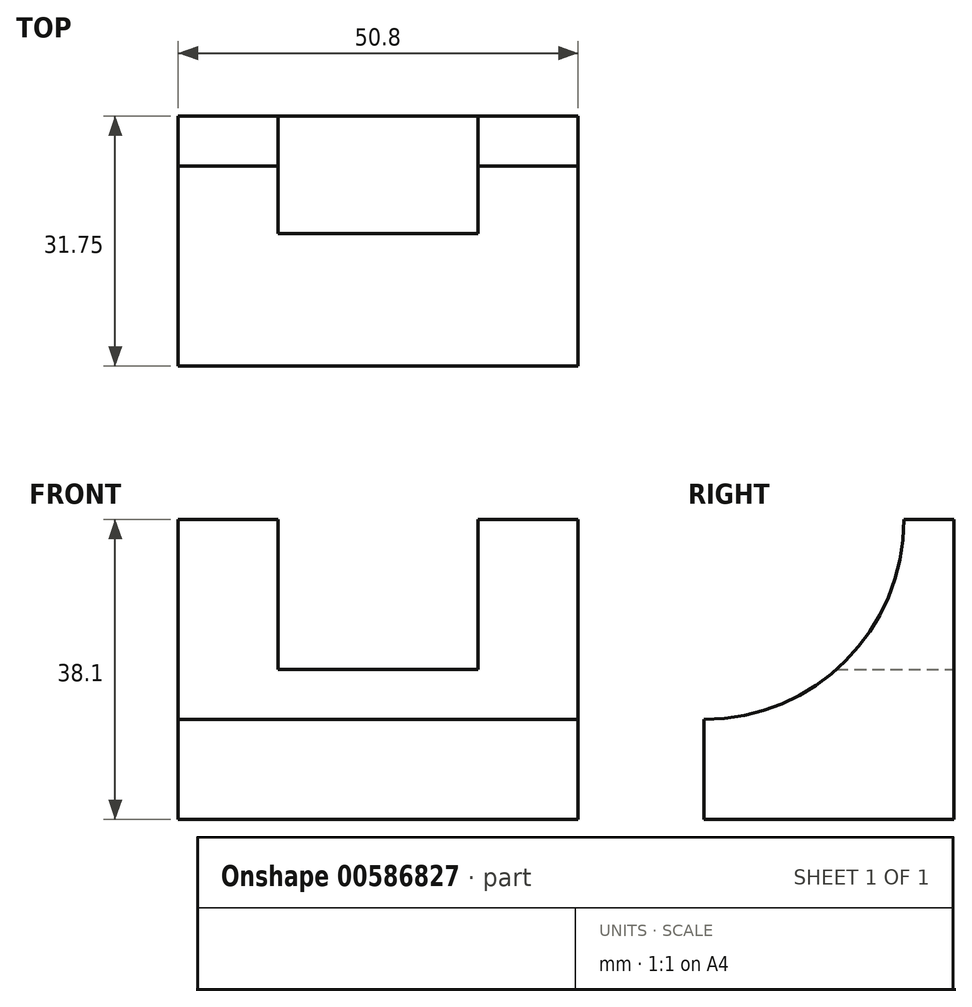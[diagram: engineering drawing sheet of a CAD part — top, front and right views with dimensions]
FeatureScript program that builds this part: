
annotation { "Feature Type Name" : "Feature", "Feature Type Description" : "" }
export const myFeature = defineFeature(function(context is Context, id is Id, definition is map)
    precondition{}
    {
        {
            var Q0;
            Q0=qCreatedBy(makeId("Right.planeOp"),FACE);
            var sketch = newSketch(context, id + "F0", { "sketchPlane" : qUnion([Q0])});
            skLineSegment(sketch, "E0", {"start": v(-49.9, 49.64) * mm, "end": v(-18.16, 49.64) * mm});
            skLineSegment(sketch, "E1", {"start": v(-18.16, 49.64) * mm, "end": v(-18.16, 11.54) * mm});
            skLineSegment(sketch, "E2", {"start": v(-18.16, 11.54) * mm, "end": v(-49.9, 11.54) * mm});
            skLineSegment(sketch, "E3", {"start": v(-49.9, 11.54) * mm, "end": v(-49.9, 49.64) * mm});
            skSolve(sketch);
        }
        {
            var Q0;
            Q0=makeQuery(id+"F0.imprint","IMPRINT",FACE,{"disambiguationData":[TD([[makeQuery(id+"F0.imprint","IMPRINT",EDGE,{"derivedFrom":sQuery(id+"F0.wireOp",EDGE,"E0")}),-1.0]])]});
            extrude(context, id + "F1", {"entities" : qUnion([Q0]), "depth" : 50.8 * mm, "offsetDistance" : 25.4 * mm});
        }
        {
            var Q0;
            Q0=makeQuery(id+"F1.opExtrude","CAP_FACE",FACE,{"disambiguationData":[OSD([sQuery(id+"F0.wireOp",EDGE,"E0"),sQuery(id+"F0.wireOp",EDGE,"E1"),sQuery(id+"F0.wireOp",EDGE,"E2"),sQuery(id+"F0.wireOp",EDGE,"E3")])],"isStart":false});
            var sketch = newSketch(context, id + "F2", { "sketchPlane" : qUnion([Q0])});
            skArc(sketch, "E4", {"start": v(-49.9, 24.24) * mm, "mid": v(-31.95, 31.68) * mm, "end": v(-24.5, 49.64) * mm});
            skSolve(sketch);
        }
        {
            var Q0;
            {var subQ0=sQuery(id+"F2.wireOp",EDGE,"E4");Q0=makeQuery(id+"F2.imprint","IMPRINT",FACE,{"disambiguationData":[TD([[makeQuery(id+"F2.imprint","IMPRINT",EDGE,{"derivedFrom":subQ0}),1.0]])]});}
            extrude(context, id + "F3", {"entities" : qUnion([Q0]), "operationType" : NewBodyOperationType.REMOVE, "endBound" : BoundingType.THROUGH_ALL, "oppositeDirection" : true, "depth" : 25.4 * mm, "offsetDistance" : 25.4 * mm});
        }
        {
            var Q0;
            Q0=makeQuery(id+"F1.opExtrude","SWEPT_FACE",FACE,{"disambiguationData":[OSD([sQuery(id+"F0.wireOp",EDGE,"E1")])]});
            var sketch = newSketch(context, id + "F4", { "sketchPlane" : qUnion([Q0])});
            skLineSegment(sketch, "E5", {"start": v(-38.1, 49.64) * mm, "end": v(-38.1, 30.6) * mm});
            skLineSegment(sketch, "E6", {"start": v(-38.1, 30.6) * mm, "end": v(-12.7, 30.6) * mm});
            skLineSegment(sketch, "E7", {"start": v(-12.7, 30.6) * mm, "end": v(-12.7, 49.64) * mm});
            skSolve(sketch);
        }
        {
            var Q0;
            {var subQ0=sQuery(id+"F4.wireOp",EDGE,"E5");Q0=makeQuery(id+"F4.imprint","IMPRINT",FACE,{"disambiguationData":[TD([[makeQuery(id+"F4.imprint","IMPRINT",EDGE,{"derivedFrom":subQ0}),1.0]])]});}
            extrude(context, id + "F5", {"entities" : qUnion([Q0]), "operationType" : NewBodyOperationType.REMOVE, "endBound" : BoundingType.THROUGH_ALL, "oppositeDirection" : true, "depth" : 25.4 * mm, "offsetDistance" : 25.4 * mm});
        }
    });
